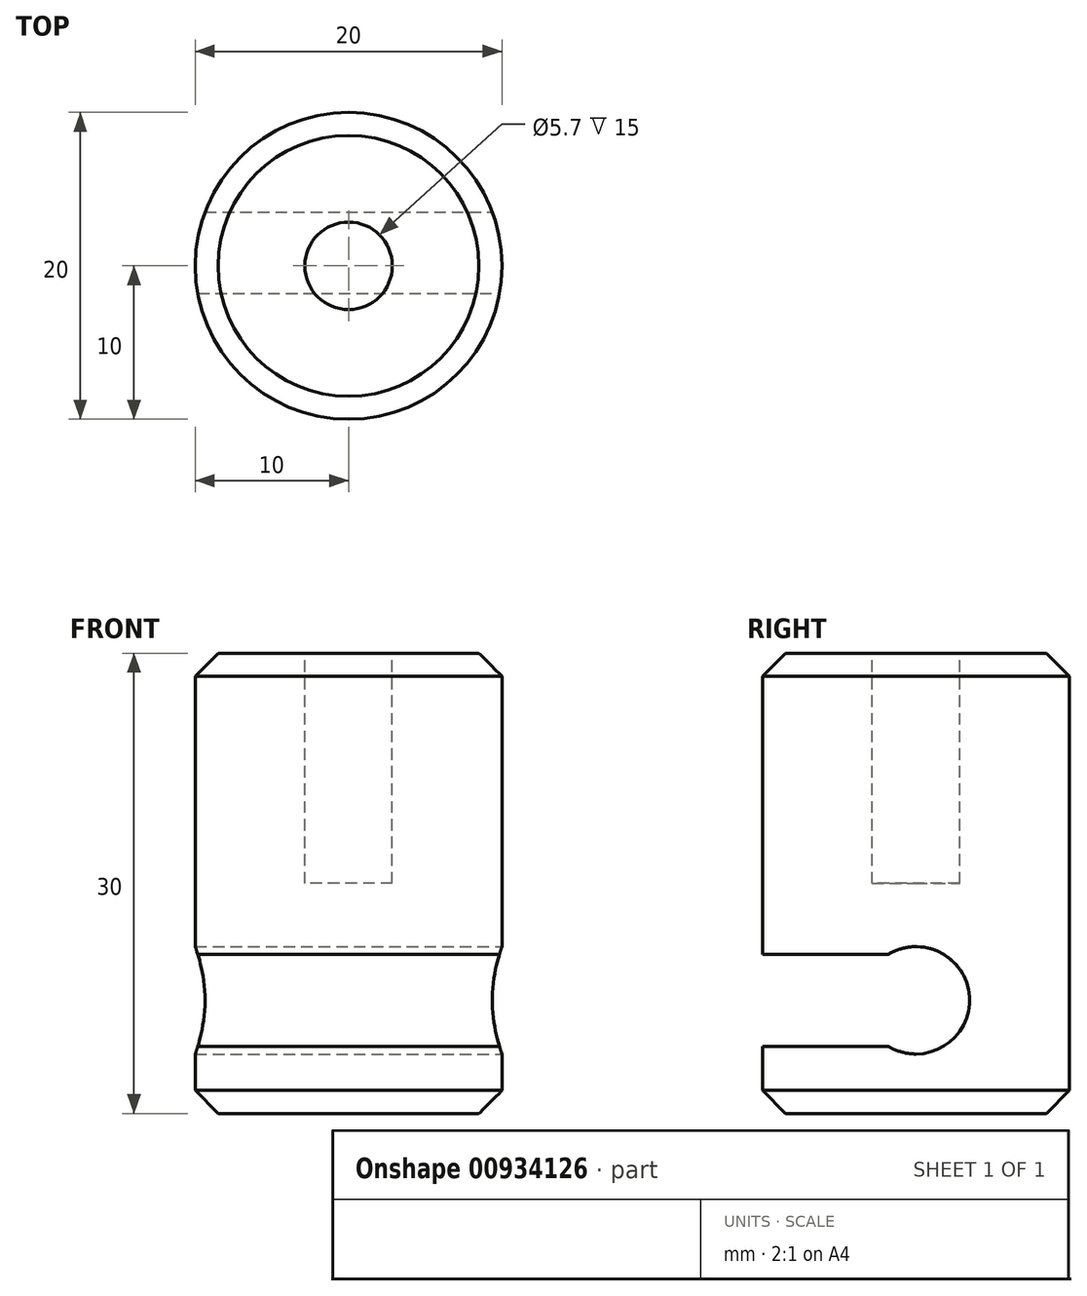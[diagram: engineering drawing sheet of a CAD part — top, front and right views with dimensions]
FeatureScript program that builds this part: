
annotation { "Feature Type Name" : "Feature", "Feature Type Description" : "" }
export const myFeature = defineFeature(function(context is Context, id is Id, definition is map)
    precondition{}
    {
        {
            var Q0;
            Q0=qCreatedBy(makeId("Top.planeOp"),FACE);
            var sketch = newSketch(context, id + "F0", { "sketchPlane" : qUnion([Q0])});
            skCircle(sketch, "E0", {"center": v(0, 0) * mm, "radius": 10 * mm});
            skSolve(sketch);
        }
        {
            var Q0;
            Q0=makeQuery(id+"F0.imprint","IMPRINT",FACE,{"disambiguationData":[TD([[makeQuery(id+"F0.imprint","IMPRINT",EDGE,{"derivedFrom":sQuery(id+"F0.wireOp",EDGE,"E0")}),1.0]])]});
            extrude(context, id + "F1", {"entities" : qUnion([Q0]), "oppositeDirection" : true, "depth" : 30 * mm, "offsetDistance" : 25 * mm});
        }
        {
            var Q0;
            Q0=makeQuery(id+"F1.opExtrude","CAP_FACE",FACE,{"disambiguationData":[OSD([sQuery(id+"F0.wireOp",EDGE,"E0")])],"isStart":true});
            var sketch = newSketch(context, id + "F2", { "sketchPlane" : qUnion([Q0])});
            skCircle(sketch, "E1", {"center": v(0, 0) * mm, "radius": 2.85 * mm});
            skSolve(sketch);
        }
        {
            var Q0;
            Q0=makeQuery(id+"F2.imprint","IMPRINT",FACE,{"disambiguationData":[TD([[makeQuery(id+"F2.imprint","IMPRINT",EDGE,{"derivedFrom":sQuery(id+"F2.wireOp",EDGE,"E1")}),1.0]])]});
            extrude(context, id + "F3", {"entities" : qUnion([Q0]), "operationType" : NewBodyOperationType.REMOVE, "oppositeDirection" : true, "depth" : 15 * mm, "offsetDistance" : 25 * mm});
        }
        {
            var Q0;
            Q0=qCreatedBy(makeId("Right.planeOp"),FACE);
            var sketch = newSketch(context, id + "F4", { "sketchPlane" : qUnion([Q0])});
            skCircle(sketch, "E2", {"center": v(0, -22.62) * mm, "radius": 3.5 * mm});
            skSolve(sketch);
        }
        {
            var Q0;
            Q0=qSketchRegion(id+"F4",true);
            extrude(context, id + "F5", {"entities" : qUnion([Q0]), "operationType" : NewBodyOperationType.REMOVE, "oppositeDirection" : true, "depth" : 10 * mm, "offsetDistance" : 25 * mm, "hasSecondDirection" : true, "secondDirectionOppositeDirection" : false, "secondDirectionDepth" : 10 * mm});
        }
        {
            var Q0;
            Q0=qCreatedBy(makeId("Front.planeOp"),FACE);
            var sketch = newSketch(context, id + "F6", { "sketchPlane" : qUnion([Q0])});
            skLineSegment(sketch, "E3", {"start": v(-20.45, -22.62) * mm, "end": v(19.13, -22.62) * mm, "construction": true});
            skSolve(sketch);
        }
        {
            var Q0;
            Q0=qCreatedBy(makeId("Right.planeOp"),FACE);
            var sketch = newSketch(context, id + "F7", { "sketchPlane" : qUnion([Q0])});
            skLineSegment(sketch, "E4.bottom", {"start": v(0, -19.62) * mm, "end": v(-11.93, -19.62) * mm});
            skLineSegment(sketch, "E4.top", {"start": v(0, -25.63) * mm, "end": v(-11.93, -25.63) * mm});
            skLineSegment(sketch, "E4.right", {"start": v(-11.93, -19.62) * mm, "end": v(-11.93, -25.63) * mm});
            skPoint(sketch, "E4.middle", {"position": v(0, -22.62) * mm});
            skLineSegment(sketch, "E5", {"start": v(0, -19.62) * mm, "end": v(0, -25.63) * mm});
            skSolve(sketch);
        }
        {
            var Q0;
            Q0=makeQuery(id+"F7.imprint","IMPRINT",FACE,{"disambiguationData":[TD([[makeQuery(id+"F7.imprint","IMPRINT",EDGE,{"derivedFrom":sQuery(id+"F7.wireOp",EDGE,"E4.bottom")}),1.0]])]});
            extrude(context, id + "F8", {"entities" : qUnion([Q0]), "operationType" : NewBodyOperationType.REMOVE, "oppositeDirection" : true, "depth" : 10 * mm, "offsetDistance" : 25 * mm, "hasSecondDirection" : true, "secondDirectionOppositeDirection" : false, "secondDirectionDepth" : 10 * mm});
        }
        {
            var Q0;
            Q0=makeQuery(id+"F3.boolean.opBoolean","COPY",EDGE,{"derivedFrom":makeQuery(id+"F3.opExtrude","CAP_EDGE",EDGE,{"disambiguationData":[OSD([sQuery(id+"F2.wireOp",EDGE,"E1")])],"isStart":true})});
            var Q1;
            Q1=makeQuery(id+"F1.opExtrude","CAP_EDGE",EDGE,{"disambiguationData":[OSD([sQuery(id+"F0.wireOp",EDGE,"E0")])],"isStart":true});
            var Q2;
            Q2=makeQuery(id+"F1.opExtrude","CAP_EDGE",EDGE,{"disambiguationData":[OSD([sQuery(id+"F0.wireOp",EDGE,"E0")])],"isStart":false});
            chamfer(context, id + "F9", {"entities" : qUnion([Q0, Q1, Q2]), "width" : 1.5 * mm, "tangentPropagation" : true});
        }
    });
